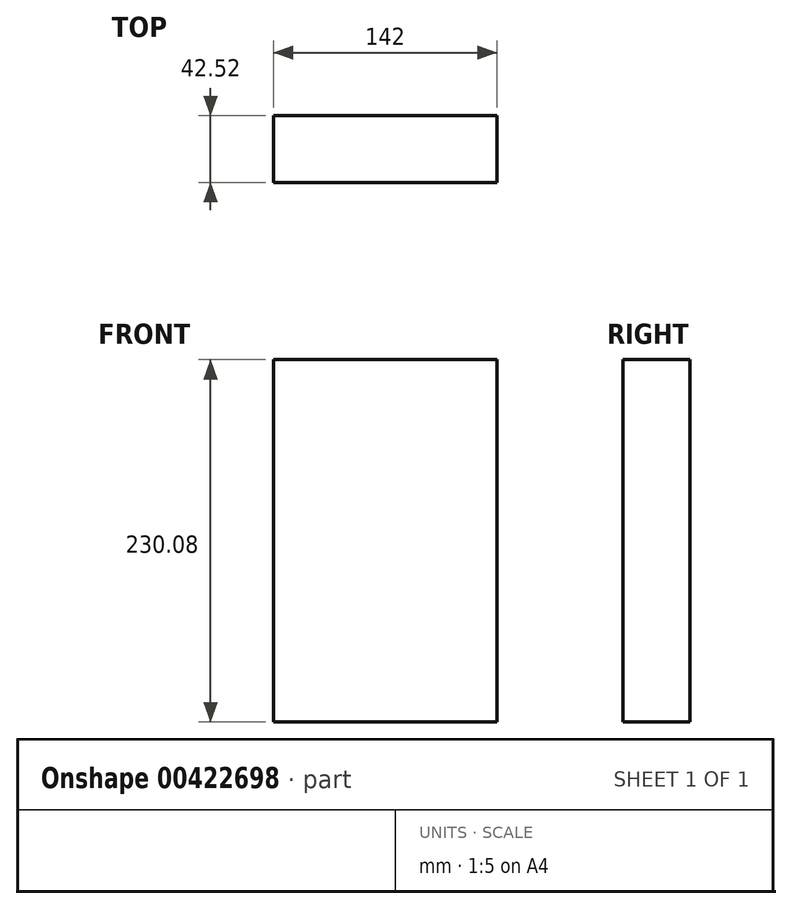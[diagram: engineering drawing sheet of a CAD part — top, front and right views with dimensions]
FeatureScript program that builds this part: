
annotation { "Feature Type Name" : "Feature", "Feature Type Description" : "" }
export const myFeature = defineFeature(function(context is Context, id is Id, definition is map)
    precondition{}
    {
        {
            var Q0;
            Q0=qCreatedBy(makeId("Front.planeOp"),FACE);
            var sketch = newSketch(context, id + "F0", { "sketchPlane" : qUnion([Q0])});
            skLineSegment(sketch, "E0", {"start": v(-123, -114.98) * mm, "end": v(-227.04, -10.5) * mm});
            skLineSegment(sketch, "E1", {"start": v(-227.04, -10.5) * mm, "end": v(-227.04, 10.5) * mm});
            skLineSegment(sketch, "E2", {"start": v(-227.04, 10.5) * mm, "end": v(-123.04, 115.02) * mm});
            skLineSegment(sketch, "E3", {"start": v(-123.04, 115.02) * mm, "end": v(122.96, 115.02) * mm});
            skLineSegment(sketch, "E4", {"start": v(122.96, 115.02) * mm, "end": v(226.96, 10.5) * mm});
            skLineSegment(sketch, "E5", {"start": v(226.96, 10.5) * mm, "end": v(226.96, -10.5) * mm});
            skLineSegment(sketch, "E6", {"start": v(226.96, -10.5) * mm, "end": v(123, -115.06) * mm});
            skLineSegment(sketch, "E7", {"start": v(123, -115.06) * mm, "end": v(-123, -114.98) * mm});
            skLineSegment(sketch, "E8", {"start": v(154.06, 0) * mm, "end": v(-382.25, 0) * mm, "construction": true});
            skPoint(sketch, "E8.startSnap0", {"position": v(226.96, 0) * mm});
            skPoint(sketch, "E8.endSnap0", {"position": v(-227.04, 0) * mm});
            skPoint(sketch, "E9.endSnap0", {"position": v(0, -115.02) * mm});
            skLineSegment(sketch, "E10", {"start": v(0, -111.59) * mm, "end": v(0, 209.86) * mm, "construction": true});
            skPoint(sketch, "E11", {"position": v(0, 0) * mm});
            skSolve(sketch);
        }
        {
            var Q0;
            Q0=qCreatedBy(makeId("Right.planeOp"),FACE);
            var sketch = newSketch(context, id + "F1", { "sketchPlane" : qUnion([Q0])});
            skPoint(sketch, "E12.0", {"position": v(0, 115.02) * mm});
            skPoint(sketch, "E13.0", {"position": v(0, 10.5) * mm});
            skPoint(sketch, "E14.0", {"position": v(0, -10.5) * mm});
            skPoint(sketch, "E15.0", {"position": v(0, -115.06) * mm});
            skLineSegment(sketch, "E16.bottom", {"start": v(0, 115.02) * mm, "end": v(-42.52, 115.02) * mm});
            skLineSegment(sketch, "E16.top", {"start": v(0, -115.06) * mm, "end": v(-42.52, -115.06) * mm});
            skLineSegment(sketch, "E16.left", {"start": v(0, 115.02) * mm, "end": v(0, -115.06) * mm});
            skLineSegment(sketch, "E16.right", {"start": v(-42.52, 115.02) * mm, "end": v(-42.52, -115.06) * mm});
            skLineSegment(sketch, "E17.bottom", {"start": v(-42.52, 115.02) * mm, "end": v(-90.75, 115.02) * mm});
            skLineSegment(sketch, "E17.top", {"start": v(-42.52, -115.06) * mm, "end": v(-90.75, -115.06) * mm});
            skLineSegment(sketch, "E17.right", {"start": v(-90.75, 115.02) * mm, "end": v(-90.75, -115.06) * mm});
            skSolve(sketch);
        }
        {
            var Q0;
            Q0=makeQuery(id+"F1.imprint","IMPRINT",FACE,{"disambiguationData":[TD([[makeQuery(id+"F1.imprint","IMPRINT",EDGE,{"derivedFrom":sQuery(id+"F1.wireOp",EDGE,"E16.bottom")}),1.0]])]});
            extrude(context, id + "F2", {"entities" : qUnion([Q0]), "oppositeDirection" : true, "depth" : 142 * mm});
        }
    });
